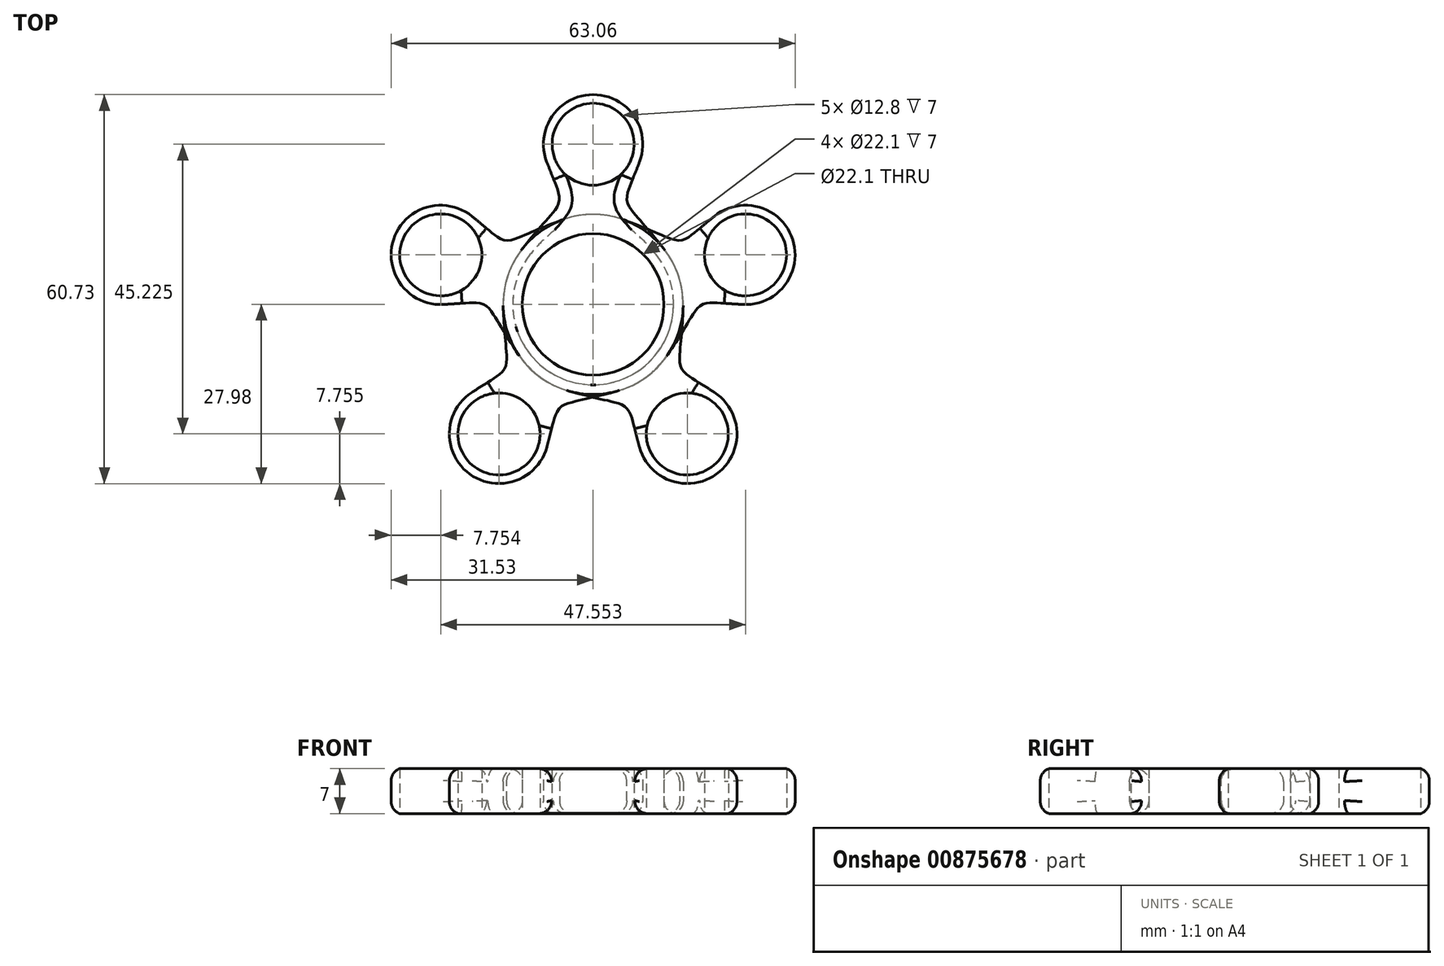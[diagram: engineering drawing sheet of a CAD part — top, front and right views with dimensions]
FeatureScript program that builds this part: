
annotation { "Feature Type Name" : "Feature", "Feature Type Description" : "" }
export const myFeature = defineFeature(function(context is Context, id is Id, definition is map)
    precondition{}
    {
        {
            var Q0;
            Q0=qCreatedBy(makeId("Top.planeOp"),FACE);
            var sketch = newSketch(context, id + "F0", { "sketchPlane" : qUnion([Q0])});
            skCircle(sketch, "E0", {"center": v(0, 0) * mm, "radius": 11.05 * mm});
            skArc(sketch, "E1.0", {"start": v(-11.02, 8.7) * mm, "mid": v(0, -14.05) * mm, "end": v(11.02, 8.7) * mm});
            skArc(sketch, "E2", {"start": v(7.23, 22.21) * mm, "mid": v(0, 32.75) * mm, "end": v(-7.23, 22.21) * mm});
            skFitSpline(sketch, "E3", {"points": [v(-7.23, 22.21) * mm, v(-11.02, 8.7) * mm], "startDerivative": vector(9.23, -23.97) * mm, "endDerivative": vector(-20.6, -26.09) * mm});
            skFitSpline(sketch, "E4.MirrorCS", {"points": [v(7.23, 22.21) * mm, v(11.02, 8.7) * mm], "startDerivative": vector(-9.23, -23.97) * mm, "endDerivative": vector(20.6, -26.09) * mm});
            skPoint(sketch, "E5", {"position": v(-18.7, 11.8) * mm});
            skPoint(sketch, "E6", {"position": v(24.7, 14.97) * mm});
            skCircle(sketch, "E7", {"center": v(0, 25) * mm, "radius": 6.4 * mm});
            skSolve(sketch);
        }
        {
            var Q0;
            Q0 = qSketchRegion(id + "F0", true);
            extrude(context, id + "F1", {"entities" : qUnion([Q0]), "endBound" : BoundingType.SYMMETRIC, "depth" : 7 * mm, "offsetDistance" : 25 * mm});
        }
        {
            var Q0;
            Q0=makeQuery(id+"Ftmiib0ERZksbMy_0.opRevolve","SWEPT_BODY",BODY,{"disambiguationData":[OSD([sQuery(id+"F0.wireOp",EDGE,"ruhPlSWM-WkIL-6jUs-lirL-jqjyKtOqKdrT")])]});
            var Q1;
            Q1=makeQuery(id+"F1.opExtrude","SWEPT_BODY",BODY,{"disambiguationData":[OSD([sQuery(id+"F0.wireOp",EDGE,"E0"),sQuery(id+"F0.wireOp",EDGE,"E1.0"),sQuery(id+"F0.wireOp",EDGE,"E2"),sQuery(id+"F0.wireOp",EDGE,"E3"),sQuery(id+"F0.wireOp",EDGE,"E4.MirrorCS"),sQuery(id+"F0.wireOp",EDGE,"ruhPlSWM-WkIL-6jUs-lirL-jqjyKtOqKdrT"),sQuery(id+"F0.wireOp",EDGE,"0Kq3n4td-lCq8-AhNw-VHQs-4hSdO0V7PoW8")])]});
            var Q2;
            Q2=makeQuery(id+"F1.opExtrude","CAP_EDGE",EDGE,{"disambiguationData":[OSD([sQuery(id+"F0.wireOp",EDGE,"E0")])],"isStart":false});
            circularPattern(context, id + "F2", {"entities" : qUnion([Q0, Q1]), "axis" : qUnion([Q2]), "angle" : 360 * degree, "instanceCount" : 5, "equalSpace" : true});
        }
        {
            var Q0;
            Q0=makeQuery(id+"F2.opPattern","COPY",EDGE,{"derivedFrom":makeQuery(id+"F1.opExtrude","CAP_EDGE",EDGE,{"disambiguationData":[OSD([sQuery(id+"F0.wireOp",EDGE,"E2")])],"isStart":false}),"instanceName":"3"});
            var Q1;
            Q1=makeQuery(id+"F2.opPattern","COPY",EDGE,{"derivedFrom":makeQuery(id+"F1.opExtrude","CAP_EDGE",EDGE,{"disambiguationData":[OSD([sQuery(id+"F0.wireOp",EDGE,"E2")])],"isStart":false}),"instanceName":"4"});
            var Q2;
            Q2=makeQuery(id+"F2.opPattern","COPY",EDGE,{"derivedFrom":makeQuery(id+"F1.opExtrude","CAP_EDGE",EDGE,{"disambiguationData":[OSD([sQuery(id+"F0.wireOp",EDGE,"E2")])],"isStart":false}),"instanceName":"2"});
            var Q3;
            Q3=makeQuery(id+"F2.opPattern","COPY",EDGE,{"derivedFrom":makeQuery(id+"F1.opExtrude","CAP_EDGE",EDGE,{"disambiguationData":[OSD([sQuery(id+"F0.wireOp",EDGE,"E2")])],"isStart":false}),"instanceName":"1"});
            var Q4;
            Q4=makeQuery(id+"F1.opExtrude","CAP_EDGE",EDGE,{"disambiguationData":[OSD([sQuery(id+"F0.wireOp",EDGE,"E2")])],"isStart":false});
            var Q5;
            Q5=makeQuery(id+"F2.opPattern","COPY",EDGE,{"derivedFrom":makeQuery(id+"F1.opExtrude","CAP_EDGE",EDGE,{"disambiguationData":[OSD([sQuery(id+"F0.wireOp",EDGE,"E2")])],"isStart":true}),"instanceName":"4"});
            var Q6;
            Q6=makeQuery(id+"F1.opExtrude","CAP_EDGE",EDGE,{"disambiguationData":[OSD([sQuery(id+"F0.wireOp",EDGE,"E2")])],"isStart":true});
            var Q7;
            Q7=makeQuery(id+"F2.opPattern","COPY",EDGE,{"derivedFrom":makeQuery(id+"F1.opExtrude","CAP_EDGE",EDGE,{"disambiguationData":[OSD([sQuery(id+"F0.wireOp",EDGE,"E2")])],"isStart":true}),"instanceName":"1"});
            var Q8;
            Q8=makeQuery(id+"F2.opPattern","COPY",EDGE,{"derivedFrom":makeQuery(id+"F1.opExtrude","CAP_EDGE",EDGE,{"disambiguationData":[OSD([sQuery(id+"F0.wireOp",EDGE,"E2")])],"isStart":true}),"instanceName":"3"});
            var Q9;
            Q9=makeQuery(id+"F2.opPattern","COPY",EDGE,{"derivedFrom":makeQuery(id+"F1.opExtrude","CAP_EDGE",EDGE,{"disambiguationData":[OSD([sQuery(id+"F0.wireOp",EDGE,"E2")])],"isStart":true}),"instanceName":"2"});
            var Q10;
            Q10=makeQuery(id+"F1.opExtrude","CAP_EDGE",EDGE,{"disambiguationData":[OSD([sQuery(id+"F0.wireOp",EDGE,"E0")])],"isStart":true});
            var Q11;
            Q11=makeQuery(id+"F1.opExtrude","CAP_EDGE",EDGE,{"disambiguationData":[OSD([sQuery(id+"F0.wireOp",EDGE,"E0")])],"isStart":false});
            fillet(context, id + "F3", {"entities" : qUnion([Q0, Q1, Q2, Q3, Q4, Q5, Q6, Q7, Q8, Q9, Q10, Q11]), "radius" : 2 * mm, "tangentPropagation" : true, "allowEdgeOverflow" : false});
        }
    });
